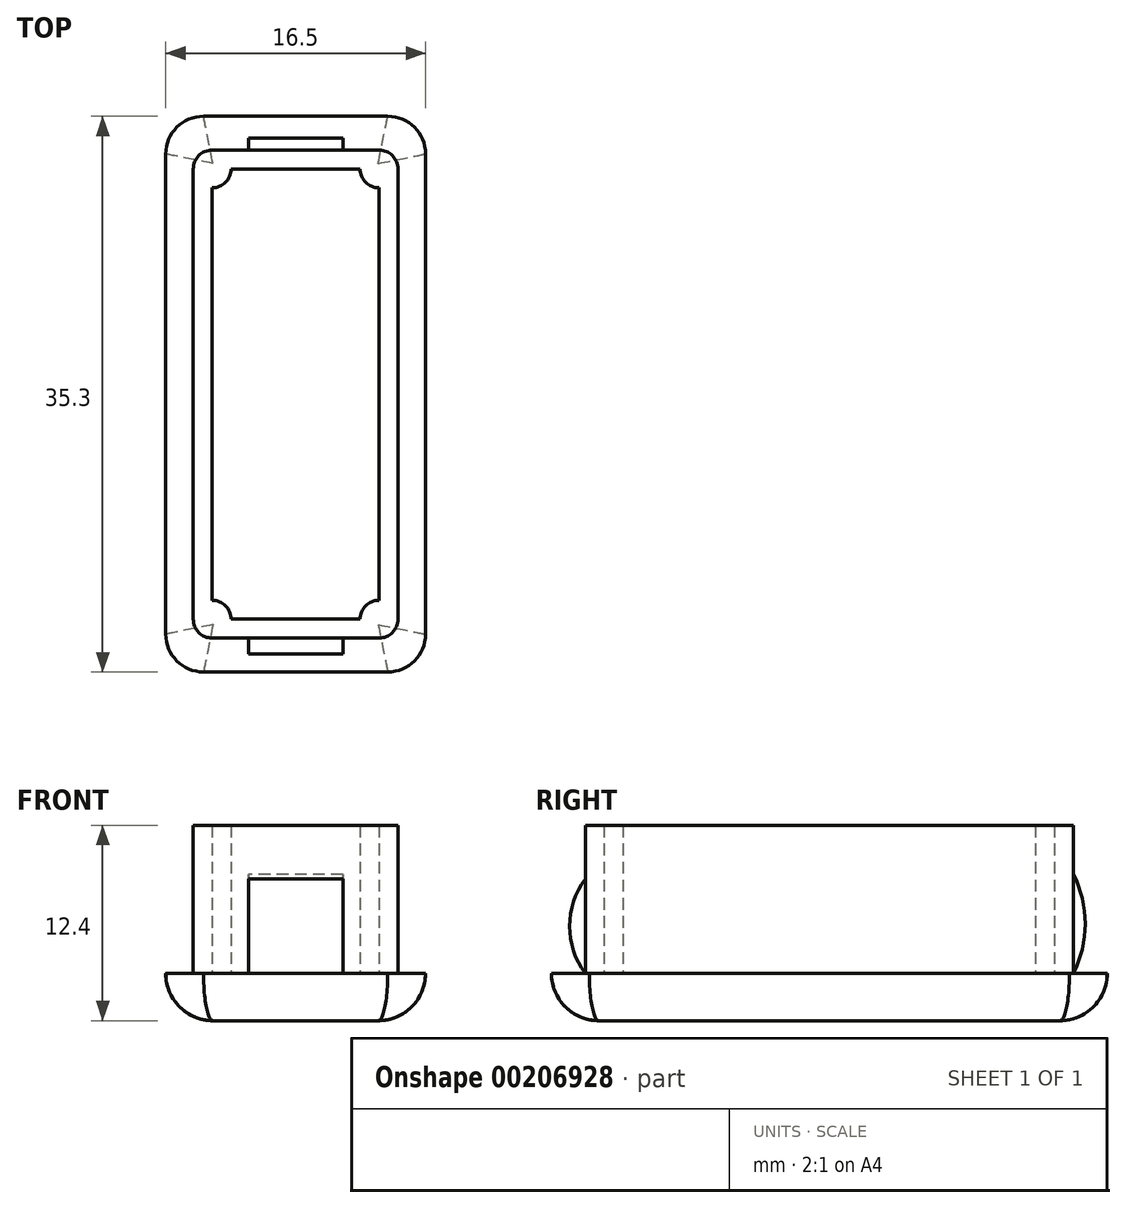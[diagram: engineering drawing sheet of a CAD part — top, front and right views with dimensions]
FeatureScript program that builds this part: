
annotation { "Feature Type Name" : "Feature", "Feature Type Description" : "" }
export const myFeature = defineFeature(function(context is Context, id is Id, definition is map)
    precondition{}
    {
        {
            var Q0;
            Q0=qCreatedBy(makeId("Top.planeOp"),FACE);
            var sketch = newSketch(context, id + "F0", { "sketchPlane" : qUnion([Q0])});
            skLineSegment(sketch, "E0.bottom", {"start": v(5.85, 17.65) * mm, "end": v(-5.85, 17.65) * mm});
            skLineSegment(sketch, "E0.top", {"start": v(5.85, -17.65) * mm, "end": v(-5.85, -17.65) * mm});
            skLineSegment(sketch, "E0.left", {"start": v(8.25, 15.25) * mm, "end": v(8.25, -15.25) * mm});
            skLineSegment(sketch, "E0.right", {"start": v(-8.25, 15.25) * mm, "end": v(-8.25, -15.25) * mm});
            skPoint(sketch, "E0.middle", {"position": v(0, 0) * mm});
            skLineSegment(sketch, "E1.bottom", {"start": v(5.3, 14.3) * mm, "end": v(-5.3, 14.3) * mm});
            skLineSegment(sketch, "E1.top", {"start": v(5.3, -14.3) * mm, "end": v(-5.3, -14.3) * mm});
            skLineSegment(sketch, "E1.left", {"start": v(5.3, 14.3) * mm, "end": v(5.3, -14.3) * mm});
            skLineSegment(sketch, "E1.right", {"start": v(-5.3, 14.3) * mm, "end": v(-5.3, -14.3) * mm});
            skCircle(sketch, "E2", {"center": v(-5.3, 14.3) * mm, "radius": 1.2 * mm});
            skPoint(sketch, "E3.right.start.orphan", {"position": v(-6.5, 15.5) * mm});
            skCircle(sketch, "E4", {"center": v(5.3, 14.3) * mm, "radius": 1.2 * mm});
            skPoint(sketch, "E3.left.start.orphan", {"position": v(6.5, 15.5) * mm});
            skCircle(sketch, "E5", {"center": v(5.3, -14.3) * mm, "radius": 1.2 * mm});
            skCircle(sketch, "E6", {"center": v(-5.3, -14.3) * mm, "radius": 1.2 * mm});
            skPoint(sketch, "E3.top.start.orphan", {"position": v(6.5, -15.5) * mm});
            skPoint(sketch, "E7.end.orphan", {"position": v(-6.5, -15.5) * mm});
            skPoint(sketch, "E8.visualSharp", {"position": v(-8.25, 17.65) * mm});
            skArc(sketch, "E8.filletArc", {"start": v(-5.85, 17.65) * mm, "mid": v(-7.55, 16.95) * mm, "end": v(-8.25, 15.25) * mm});
            skPoint(sketch, "E9.visualSharp", {"position": v(8.25, 17.65) * mm});
            skArc(sketch, "E9.filletArc", {"start": v(8.25, 15.25) * mm, "mid": v(7.55, 16.95) * mm, "end": v(5.85, 17.65) * mm});
            skPoint(sketch, "E10.visualSharp", {"position": v(-8.25, -17.65) * mm});
            skArc(sketch, "E10.filletArc", {"start": v(-8.25, -15.25) * mm, "mid": v(-7.55, -16.95) * mm, "end": v(-5.85, -17.65) * mm});
            skPoint(sketch, "E11.visualSharp", {"position": v(8.25, -17.65) * mm});
            skArc(sketch, "E11.filletArc", {"start": v(5.85, -17.65) * mm, "mid": v(7.55, -16.95) * mm, "end": v(8.25, -15.25) * mm});
            skLineSegment(sketch, "E12.bottom", {"start": v(5.3, 15.5) * mm, "end": v(-5.3, 15.5) * mm});
            skLineSegment(sketch, "E12.top", {"start": v(5.3, -15.5) * mm, "end": v(-5.3, -15.5) * mm});
            skLineSegment(sketch, "E12.left", {"start": v(6.5, 14.3) * mm, "end": v(6.5, -14.3) * mm});
            skLineSegment(sketch, "E12.right", {"start": v(-6.5, 14.3) * mm, "end": v(-6.5, -14.3) * mm});
            skArc(sketch, "E13.filletArc", {"start": v(6.5, 14.3) * mm, "mid": v(6.15, 15.15) * mm, "end": v(5.3, 15.5) * mm});
            skArc(sketch, "E14.filletArc", {"start": v(-5.3, 15.5) * mm, "mid": v(-6.15, 15.15) * mm, "end": v(-6.5, 14.3) * mm});
            skArc(sketch, "E15.filletArc", {"start": v(-6.5, -14.3) * mm, "mid": v(-6.15, -15.15) * mm, "end": v(-5.3, -15.5) * mm});
            skArc(sketch, "E16.filletArc", {"start": v(5.3, -15.5) * mm, "mid": v(6.15, -15.15) * mm, "end": v(6.5, -14.3) * mm});
            skSolve(sketch);
        }
        {
            var Q0;
            {var subQ5=sQuery(id+"F0.wireOp",EDGE,"E12.bottom");Q0=makeQuery(id+"F0.imprint","IMPRINT",FACE,{"disambiguationData":[TD([[makeQuery(id+"F0.imprint","IMPRINT",EDGE,{"derivedFrom":subQ5}),1.0]])]});}
            var Q1;
            {var subQ0=sQuery(id+"F0.wireOp",EDGE,"E1.left");var subQ1=sQuery(id+"F0.wireOp",EDGE,"E1.bottom");var subQ2=makeQuery(id+"F0.imprint","INTERSECT",VERTEX,{"derivedFrom":[subQ1,subQ0]});Q1=makeQuery(id+"F0.imprint","IMPRINT",FACE,{"disambiguationData":[TD([[makeQuery(id+"F0.imprint","IMPRINT",EDGE,{"disambiguationData":[TD([[subQ2,-1.0]])],"derivedFrom":subQ1}),-1.0]])]});}
            var Q2;
            {var subQ0=sQuery(id+"F0.wireOp",EDGE,"E1.left");var subQ1=sQuery(id+"F0.wireOp",EDGE,"E1.bottom");var subQ2=makeQuery(id+"F0.imprint","INTERSECT",VERTEX,{"derivedFrom":[subQ1,subQ0]});Q2=makeQuery(id+"F0.imprint","IMPRINT",FACE,{"disambiguationData":[TD([[makeQuery(id+"F0.imprint","IMPRINT",EDGE,{"disambiguationData":[TD([[subQ2,-1.0]])],"derivedFrom":subQ1}),1.0]])]});}
            var Q3;
            {var subQ5=sQuery(id+"F0.wireOp",EDGE,"E12.left");Q3=makeQuery(id+"F0.imprint","IMPRINT",FACE,{"disambiguationData":[TD([[makeQuery(id+"F0.imprint","IMPRINT",EDGE,{"derivedFrom":subQ5}),-1.0]])]});}
            var Q4;
            {var subQ2=sQuery(id+"F0.wireOp",EDGE,"E1.top");var subQ5=sQuery(id+"F0.wireOp",EDGE,"E1.left");var subQ7=makeQuery(id+"F0.imprint","INTERSECT",VERTEX,{"derivedFrom":[subQ2,subQ5]});Q4=makeQuery(id+"F0.imprint","IMPRINT",FACE,{"disambiguationData":[TD([[makeQuery(id+"F0.imprint","IMPRINT",EDGE,{"disambiguationData":[TD([[subQ7,-1.0]])],"derivedFrom":subQ2}),1.0]])]});}
            var Q5;
            {var subQ0=sQuery(id+"F0.wireOp",EDGE,"E1.left");var subQ1=sQuery(id+"F0.wireOp",EDGE,"E1.top");var subQ2=makeQuery(id+"F0.imprint","INTERSECT",VERTEX,{"derivedFrom":[subQ1,subQ0]});Q5=makeQuery(id+"F0.imprint","IMPRINT",FACE,{"disambiguationData":[TD([[makeQuery(id+"F0.imprint","IMPRINT",EDGE,{"disambiguationData":[TD([[subQ2,-1.0]])],"derivedFrom":subQ1}),-1.0]])]});}
            var Q6;
            {var subQ5=sQuery(id+"F0.wireOp",EDGE,"E12.top");Q6=makeQuery(id+"F0.imprint","IMPRINT",FACE,{"disambiguationData":[TD([[makeQuery(id+"F0.imprint","IMPRINT",EDGE,{"derivedFrom":subQ5}),-1.0]])]});}
            var Q7;
            {var subQ0=sQuery(id+"F0.wireOp",EDGE,"E1.right");var subQ1=sQuery(id+"F0.wireOp",EDGE,"E1.top");var subQ2=makeQuery(id+"F0.imprint","INTERSECT",VERTEX,{"derivedFrom":[subQ1,subQ0]});Q7=makeQuery(id+"F0.imprint","IMPRINT",FACE,{"disambiguationData":[TD([[makeQuery(id+"F0.imprint","IMPRINT",EDGE,{"disambiguationData":[TD([[subQ2,1.0]])],"derivedFrom":subQ1}),-1.0]])]});}
            var Q8;
            {var subQ3=sQuery(id+"F0.wireOp",EDGE,"E1.right");var subQ5=sQuery(id+"F0.wireOp",EDGE,"E1.top");var subQ6=makeQuery(id+"F0.imprint","INTERSECT",VERTEX,{"derivedFrom":[subQ5,subQ3]});Q8=makeQuery(id+"F0.imprint","IMPRINT",FACE,{"disambiguationData":[TD([[makeQuery(id+"F0.imprint","IMPRINT",EDGE,{"disambiguationData":[TD([[subQ6,1.0]])],"derivedFrom":subQ5}),1.0]])]});}
            var Q9;
            {var subQ5=sQuery(id+"F0.wireOp",EDGE,"E12.right");Q9=makeQuery(id+"F0.imprint","IMPRINT",FACE,{"disambiguationData":[TD([[makeQuery(id+"F0.imprint","IMPRINT",EDGE,{"derivedFrom":subQ5}),1.0]])]});}
            var Q10;
            {var subQ3=sQuery(id+"F0.wireOp",EDGE,"E1.right");var subQ4=sQuery(id+"F0.wireOp",EDGE,"E1.bottom");var subQ5=makeQuery(id+"F0.imprint","INTERSECT",VERTEX,{"derivedFrom":[subQ4,subQ3]});Q10=makeQuery(id+"F0.imprint","IMPRINT",FACE,{"disambiguationData":[TD([[makeQuery(id+"F0.imprint","IMPRINT",EDGE,{"disambiguationData":[TD([[subQ5,1.0]])],"derivedFrom":subQ4}),-1.0]])]});}
            var Q11;
            {var subQ0=sQuery(id+"F0.wireOp",EDGE,"E1.right");var subQ1=sQuery(id+"F0.wireOp",EDGE,"E1.bottom");var subQ2=makeQuery(id+"F0.imprint","INTERSECT",VERTEX,{"derivedFrom":[subQ1,subQ0]});Q11=makeQuery(id+"F0.imprint","IMPRINT",FACE,{"disambiguationData":[TD([[makeQuery(id+"F0.imprint","IMPRINT",EDGE,{"disambiguationData":[TD([[subQ2,1.0]])],"derivedFrom":subQ1}),1.0]])]});}
            extrude(context, id + "F1", {"entities" : qUnion([Q0, Q1, Q2, Q3, Q4, Q5, Q6, Q7, Q8, Q9, Q10, Q11]), "depth" : 12.4 * mm});
        }
        {
            var Q0;
            Q0=makeQuery(id+"F0.imprint","IMPRINT",FACE,{"disambiguationData":[TD([[makeQuery(id+"F0.imprint","IMPRINT",EDGE,{"derivedFrom":sQuery(id+"F0.wireOp",EDGE,"E0.bottom")}),1.0]])]});
            var Q1;
            {var subQ10=sQuery(id+"F0.wireOp",EDGE,"E4");var subQ13=sQuery(id+"F0.wireOp",EDGE,"E1.bottom");var subQ14=makeQuery(id+"F0.imprint","INTERSECT",VERTEX,{"derivedFrom":[subQ13,subQ10]});Q1=makeQuery(id+"F0.imprint","IMPRINT",FACE,{"disambiguationData":[TD([[makeQuery(id+"F0.imprint","IMPRINT",EDGE,{"disambiguationData":[TD([[subQ14,-1.0]])],"derivedFrom":subQ13}),1.0]])]});}
            extrude(context, id + "F2", {"entities" : qUnion([Q0, Q1]), "operationType" : NewBodyOperationType.ADD, "depth" : 3 * mm});
        }
        {
            var Q0;
            Q0=makeQuery(id+"F2.opExtrude","CAP_EDGE",EDGE,{"disambiguationData":[OSD([sQuery(id+"F0.wireOp",EDGE,"E0.top")])],"isStart":true});
            fillet(context, id + "F3", {"entities" : qUnion([Q0]), "radius" : 3 * mm, "tangentPropagation" : true, "allowEdgeOverflow" : false});
        }
        {
            var Q0;
            Q0=qCreatedBy(makeId("Right.planeOp"),FACE);
            var sketch = newSketch(context, id + "F4", { "sketchPlane" : qUnion([Q0])});
            skArc(sketch, "E17", {"start": v(-15.5, 9) * mm, "mid": v(-16.5, 6) * mm, "end": v(-15.5, 3) * mm});
            skLineSegment(sketch, "E18", {"start": v(-15.5, 9) * mm, "end": v(-15.5, 3) * mm});
            skArc(sketch, "E19", {"start": v(15.5, 3) * mm, "mid": v(16.25, 6.15) * mm, "end": v(15.5, 9.3) * mm});
            skLineSegment(sketch, "E20", {"start": v(15.5, 9.3) * mm, "end": v(15.5, 3) * mm});
            skSolve(sketch);
        }
        {
            var Q0;
            Q0 = qSketchRegion(id + "F4", true);
            extrude(context, id + "F5", {"entities" : qUnion([Q0]), "operationType" : NewBodyOperationType.ADD, "endBound" : BoundingType.SYMMETRIC, "depth" : 6 * mm});
        }
    });
